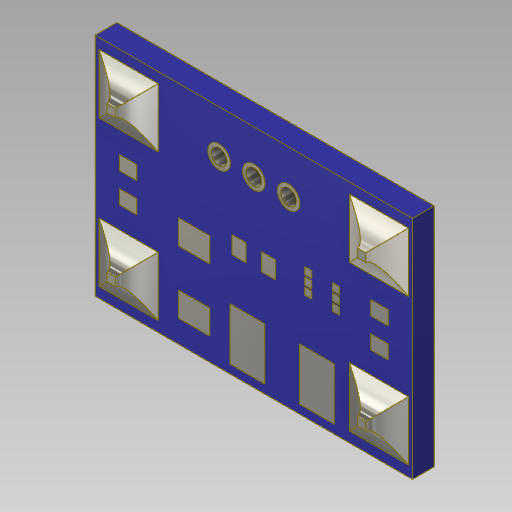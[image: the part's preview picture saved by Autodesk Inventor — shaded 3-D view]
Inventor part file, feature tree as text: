
AUTODESK INVENTOR PART (.ipt)
format: ipt  version: 2020 (Build 240168000, 168)  size: 410,112 bytes
history: native  units: in
note: dims shown in document units (in); Inventor stores cm internally (conversion verified against a paired STEP export)
features: other x8, reference x6, sketch x5, extrude x4, mirror x1, plane x1, loft x1, pattern_linear x1, projected_geometry x1
ambient origin geometry x8: Origin, YZ Plane, XZ Plane, XY Plane, X Axis, Y Axis, Z Axis, Center Point
bodies: Solid1 (feature_tree)
feature tree (28):
  extrude  "Extrusion1"  Depth=0.65in
  sketch  "Sketch2"  dims[d2=0.0625in d3=0.0in d4=0.06in]
  extrude  "Extrusion2"  Depth=0.06in
  extrude  "Extrusion3"  Depth=0.42in
  mirror  "Mirror1"
  extrude  "Extrusion4"  Depth=1.1811in
  plane  "Work Plane1"
  loft  "Loft1"
  pattern_linear  "Rectangular Pattern1"  Spacing1=0.17in  [1 undecoded]
  sketch  "Sketch1"  dims[d0=0.913in d1=0.65in]
  sketch  "Sketch3"  dims[d5=0.72in d6=0.42in]
  projected_geometry  "Projected Loop1"
  sketch  "Sketch4"  dims[d7=0.045in d8=1.1811in d10=0.1in d11=0.3937in d13=1.0in]
  reference  "Reference1"
  reference  "Reference2"
  reference  "Reference3"
  reference  "Reference4"
  sketch  "Sketch6"  dims[d15=0.125in d16=0.0625in d17=0.0in d18=0.17in d19=0.72in d20=0.42in d21=0.7874in d23=0.72in d24=0.7874in d26=0.42in d29=0.065in d30=1.1811in d32=0.1in d33=0.3937in d35=1.0in d37=0.0001in d38=0.0in d39=0.05in d40=0.04in d41=0.125in d42=0.125in d43=0.3in d44=0.07in d45=0.125in d46=0.15in d50=0.3in d51=0.1in d52=0.025in d53=0.225in d54=0.09in d55=0.07in d56=0.25in d58=0.24in d59=0.02in d60=0.02in d61=1.1811in d63=0.0256in d64=0.7874in d66=0.08in d69=0.21in d70=0.2749in d71=0.0001in d72=0.0in d73=0.315in d74=0.0256in d75=0.05in d76=0.0in d77=90.0deg d78=0.3937in d79=90.0deg d80=0.7874in d82=0.42in d83=0.7874in d85=0.72in]
  reference  "Reference5"
  reference  "Reference6"
  other  "Edges1"
  parser-record x2  (decoder bookkeeping rows leaked as tree rows — omitted from the tree; the rows remain in map.json)
  other  "Boost Converter.iam"
  other  "SOT-23 6 pin:1"
  other  "400nH Inductor:1"
  other  "Data Acquisition_R2.iam"
  other  "1 pin header:2"
note: 1 required parameter value undecoded (feature->parameter linkage not recoverable at this tier; creation-order binding heuristic only, values carry confidence <= 0.55)
note: 2 file-system paths scrubbed to <path> (originals preserved in map.json)
